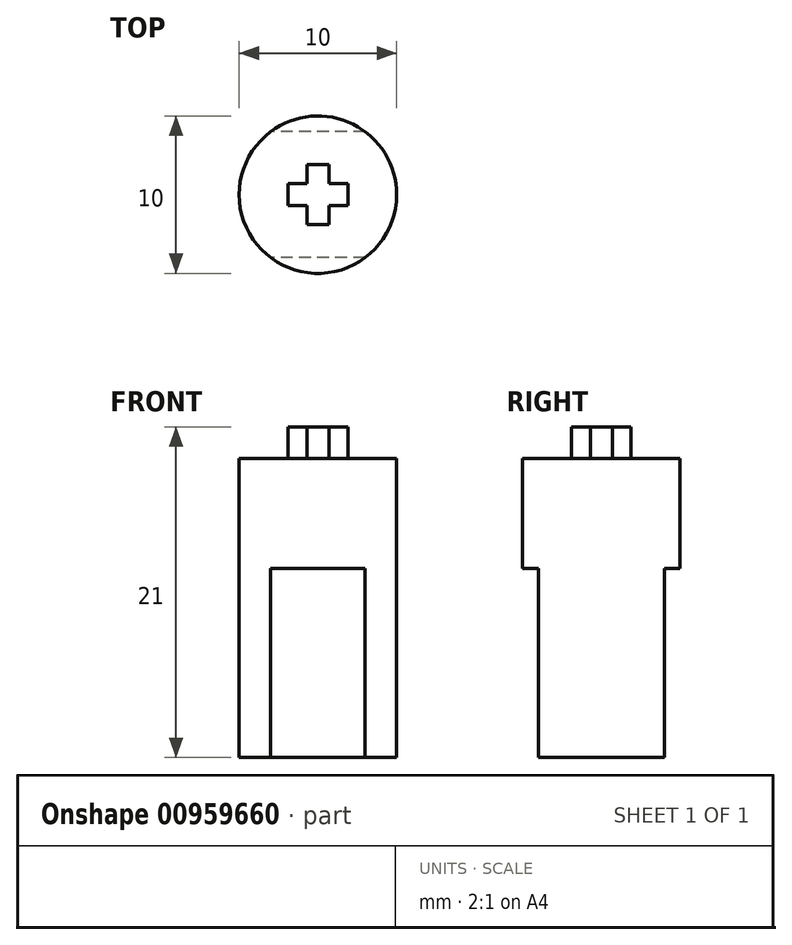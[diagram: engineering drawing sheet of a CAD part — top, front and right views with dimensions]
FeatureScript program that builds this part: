
annotation { "Feature Type Name" : "Feature", "Feature Type Description" : "" }
export const myFeature = defineFeature(function(context is Context, id is Id, definition is map)
    precondition{}
    {
        {
            var Q0;
            Q0=qCreatedBy(makeId("Top.planeOp"),FACE);
            var sketch = newSketch(context, id + "F0", { "sketchPlane" : qUnion([Q0])});
            skCircle(sketch, "E0", {"center": v(0, 0) * mm, "radius": 5 * mm});
            skSolve(sketch);
        }
        {
            var Q0;
            Q0=makeQuery(id+"F0.imprint","IMPRINT",FACE,{"disambiguationData":[TD([[makeQuery(id+"F0.imprint","IMPRINT",EDGE,{"derivedFrom":sQuery(id+"F0.wireOp",EDGE,"E0")}),1.0]])]});
            extrude(context, id + "F1", {"entities" : qUnion([Q0]), "depth" : 19 * mm, "offsetDistance" : 25 * mm});
        }
        {
            var Q0;
            Q0=makeQuery(id+"F1.opExtrude","CAP_FACE",FACE,{"disambiguationData":[OSD([sQuery(id+"F0.wireOp",EDGE,"E0")])],"isStart":true});
            var sketch = newSketch(context, id + "F2", { "sketchPlane" : qUnion([Q0])});
            skLineSegment(sketch, "E1.bottom", {"start": v(7.45, -4) * mm, "end": v(-7.45, -4) * mm});
            skLineSegment(sketch, "E1.top", {"start": v(7.45, 4) * mm, "end": v(-7.45, 4) * mm});
            skLineSegment(sketch, "E1.left", {"start": v(7.45, -4) * mm, "end": v(7.45, 4) * mm});
            skLineSegment(sketch, "E1.right", {"start": v(-7.45, -4) * mm, "end": v(-7.45, 4) * mm});
            skPoint(sketch, "E1.middle", {"position": v(0, 0) * mm});
            skSolve(sketch);
        }
        {
            var Q0;
            {var subQ0=sQuery(id+"F2.wireOp",EDGE,"E1.top");var subQ1=makeQuery(id+"F1.opExtrude","CAP_EDGE",EDGE,{"disambiguationData":[OSD([sQuery(id+"F0.wireOp",EDGE,"E0")])],"isStart":true});var subQ2=makeQuery(id+"F2.imprint","INTERSECT",VERTEX,{"disambiguationData":[OD(0.0)],"derivedFrom":[subQ1,subQ0]});Q0=makeQuery(id+"F2.imprint","IMPRINT",FACE,{"disambiguationData":[TD([[makeQuery(id+"F2.imprint","IMPRINT",EDGE,{"disambiguationData":[TD([[subQ2,-1.0]])],"derivedFrom":subQ0}),-1.0]])]});}
            var Q1;
            {var subQ0=sQuery(id+"F2.wireOp",EDGE,"E1.bottom");var subQ1=makeQuery(id+"F1.opExtrude","CAP_EDGE",EDGE,{"disambiguationData":[OSD([sQuery(id+"F0.wireOp",EDGE,"E0")])],"isStart":true});var subQ2=makeQuery(id+"F2.imprint","INTERSECT",VERTEX,{"disambiguationData":[OD(0.0)],"derivedFrom":[subQ1,subQ0]});Q1=makeQuery(id+"F2.imprint","IMPRINT",FACE,{"disambiguationData":[TD([[makeQuery(id+"F2.imprint","IMPRINT",EDGE,{"disambiguationData":[TD([[subQ2,-1.0]])],"derivedFrom":subQ0}),1.0]])]});}
            extrude(context, id + "F3", {"entities" : qUnion([Q0, Q1]), "operationType" : NewBodyOperationType.REMOVE, "oppositeDirection" : true, "depth" : 12 * mm, "offsetDistance" : 25 * mm});
        }
        {
            var Q0;
            Q0=makeQuery(id+"F1.opExtrude","CAP_FACE",FACE,{"disambiguationData":[OSD([sQuery(id+"F0.wireOp",EDGE,"E0")])],"isStart":false});
            var sketch = newSketch(context, id + "F4", { "sketchPlane" : qUnion([Q0])});
            skLineSegment(sketch, "E2.bottom", {"start": v(0.7, -1.9) * mm, "end": v(-0.7, -1.9) * mm});
            skLineSegment(sketch, "E2.top", {"start": v(0.7, 1.9) * mm, "end": v(-0.7, 1.9) * mm});
            skLineSegment(sketch, "E2.left", {"start": v(0.7, -1.9) * mm, "end": v(0.7, 1.9) * mm});
            skLineSegment(sketch, "E2.right", {"start": v(-0.7, -1.9) * mm, "end": v(-0.7, 1.9) * mm});
            skPoint(sketch, "E2.middle", {"position": v(0, 0) * mm});
            skLineSegment(sketch, "E3.bottom", {"start": v(1.9, -0.7) * mm, "end": v(-1.9, -0.7) * mm});
            skLineSegment(sketch, "E3.top", {"start": v(1.9, 0.7) * mm, "end": v(-1.9, 0.7) * mm});
            skLineSegment(sketch, "E3.left", {"start": v(1.9, -0.7) * mm, "end": v(1.9, 0.7) * mm});
            skLineSegment(sketch, "E3.right", {"start": v(-1.9, -0.7) * mm, "end": v(-1.9, 0.7) * mm});
            skSolve(sketch);
        }
        {
            var Q0;
            {var subQ0=sQuery(id+"F4.wireOp",EDGE,"E2.top");Q0=makeQuery(id+"F4.imprint","IMPRINT",FACE,{"disambiguationData":[TD([[makeQuery(id+"F4.imprint","IMPRINT",EDGE,{"derivedFrom":subQ0}),1.0]])]});}
            var Q1;
            {var subQ5=sQuery(id+"F4.wireOp",EDGE,"E3.right");Q1=makeQuery(id+"F4.imprint","IMPRINT",FACE,{"disambiguationData":[TD([[makeQuery(id+"F4.imprint","IMPRINT",EDGE,{"derivedFrom":subQ5}),-1.0]])]});}
            var Q2;
            {var subQ0=sQuery(id+"F4.wireOp",EDGE,"E3.bottom");var subQ1=sQuery(id+"F4.wireOp",EDGE,"E2.left");var subQ2=makeQuery(id+"F4.imprint","INTERSECT",VERTEX,{"derivedFrom":[subQ1,subQ0]});Q2=makeQuery(id+"F4.imprint","IMPRINT",FACE,{"disambiguationData":[TD([[makeQuery(id+"F4.imprint","IMPRINT",EDGE,{"disambiguationData":[TD([[subQ2,-1.0]])],"derivedFrom":subQ1}),1.0]])]});}
            var Q3;
            {var subQ0=sQuery(id+"F4.wireOp",EDGE,"E2.bottom");Q3=makeQuery(id+"F4.imprint","IMPRINT",FACE,{"disambiguationData":[TD([[makeQuery(id+"F4.imprint","IMPRINT",EDGE,{"derivedFrom":subQ0}),-1.0]])]});}
            var Q4;
            {var subQ5=sQuery(id+"F4.wireOp",EDGE,"E3.left");Q4=makeQuery(id+"F4.imprint","IMPRINT",FACE,{"disambiguationData":[TD([[makeQuery(id+"F4.imprint","IMPRINT",EDGE,{"derivedFrom":subQ5}),1.0]])]});}
            extrude(context, id + "F5", {"entities" : qUnion([Q0, Q1, Q2, Q3, Q4]), "operationType" : NewBodyOperationType.ADD, "depth" : 2 * mm, "offsetDistance" : 25 * mm});
        }
    });
